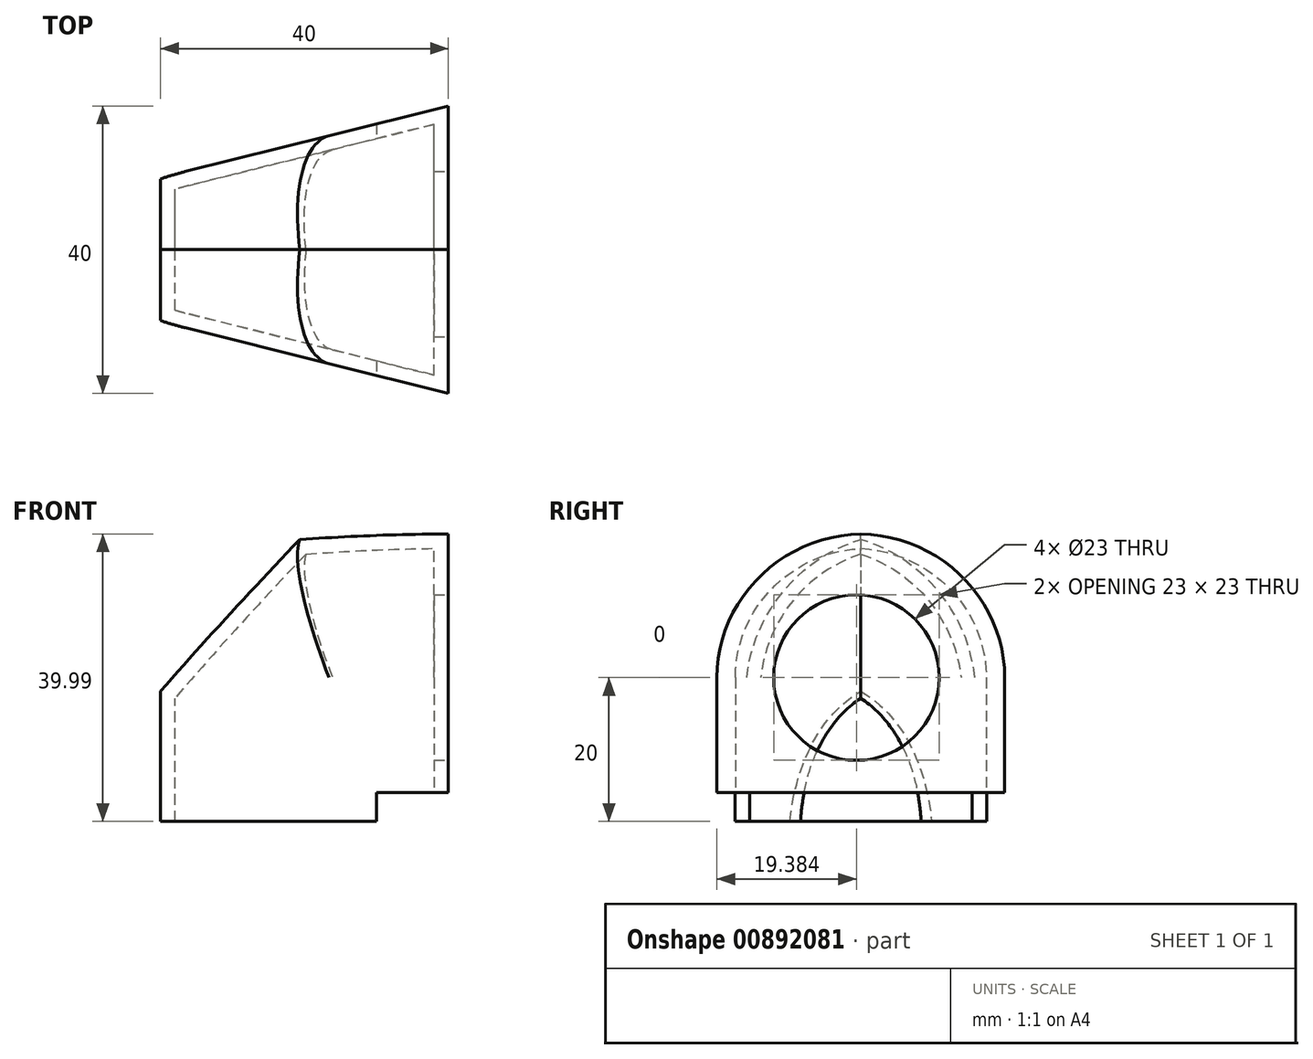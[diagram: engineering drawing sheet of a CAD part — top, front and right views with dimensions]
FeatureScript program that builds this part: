
annotation { "Feature Type Name" : "Feature", "Feature Type Description" : "" }
export const myFeature = defineFeature(function(context is Context, id is Id, definition is map)
    precondition{}
    {
        {
            var Q0;
            Q0=qCreatedBy(makeId("Top.planeOp"),FACE);
            var sketch = newSketch(context, id + "F0", { "sketchPlane" : qUnion([Q0])});
            skLineSegment(sketch, "E0", {"start": v(0, 0) * mm, "end": v(0, 40) * mm});
            skLineSegment(sketch, "E1", {"start": v(0, 20) * mm, "end": v(-79.69, 20) * mm, "construction": true});
            skLineSegment(sketch, "E2", {"start": v(-40, 10) * mm, "end": v(-40, 30) * mm});
            skLineSegment(sketch, "E3", {"start": v(-40, 30) * mm, "end": v(0, 40) * mm});
            skLineSegment(sketch, "E4", {"start": v(0, 0) * mm, "end": v(-40, 10) * mm});
            skSolve(sketch);
        }
        {
            var Q0;
            Q0=makeQuery(id+"F0.imprint","IMPRINT",FACE,{"disambiguationData":[TD([[makeQuery(id+"F0.imprint","IMPRINT",EDGE,{"derivedFrom":sQuery(id+"F0.wireOp",EDGE,"E0")}),1.0]])]});
            extrude(context, id + "F1", {"entities" : qUnion([Q0]), "depth" : 40 * mm, "offsetDistance" : 25 * mm});
        }
        {
            var Q0;
            Q0=makeQuery(id+"F1.opExtrude","CAP_EDGE",EDGE,{"disambiguationData":[OSD([sQuery(id+"F0.wireOp",EDGE,"E2")])],"isStart":false});
            chamfer(context, id + "F2", {"entities" : qUnion([Q0]), "width" : 20 * mm, "tangentPropagation" : true});
        }
        {
            var Q0;
            Q0=makeQuery(id+"F1.opExtrude","CAP_EDGE",EDGE,{"disambiguationData":[OSD([sQuery(id+"F0.wireOp",EDGE,"E3")])],"isStart":false});
            var Q1;
            Q1=makeQuery(id+"F1.opExtrude","CAP_EDGE",EDGE,{"disambiguationData":[OSD([sQuery(id+"F0.wireOp",EDGE,"E4")])],"isStart":false});
            var Q2;
            Q2=makeQuery(id+"F2.opChamfer","BLEND_EDGE",EDGE,{"blendedFrom":[makeQuery(id+"F1.opExtrude","CAP_EDGE",EDGE,{"disambiguationData":[OSD([sQuery(id+"F0.wireOp",EDGE,"E2")])],"isStart":false}),makeQuery(id+"F1.opExtrude","SWEPT_FACE",FACE,{"disambiguationData":[OSD([sQuery(id+"F0.wireOp",EDGE,"E4")])]})],"blendedInto":[makeQuery(id+"F1.opExtrude","SWEPT_FACE",FACE,{"disambiguationData":[OSD([sQuery(id+"F0.wireOp",EDGE,"E4")])]})]});
            var Q3;
            Q3=makeQuery(id+"F2.opChamfer","BLEND_EDGE",EDGE,{"blendedFrom":[makeQuery(id+"F1.opExtrude","CAP_EDGE",EDGE,{"disambiguationData":[OSD([sQuery(id+"F0.wireOp",EDGE,"E2")])],"isStart":false}),makeQuery(id+"F1.opExtrude","SWEPT_FACE",FACE,{"disambiguationData":[OSD([sQuery(id+"F0.wireOp",EDGE,"E3")])]})],"blendedInto":[makeQuery(id+"F1.opExtrude","SWEPT_FACE",FACE,{"disambiguationData":[OSD([sQuery(id+"F0.wireOp",EDGE,"E3")])]})]});
            fillet(context, id + "F3", {"entities" : qUnion([Q0, Q1, Q2, Q3]), "radius" : 20 * mm, "tangentPropagation" : true, "allowEdgeOverflow" : false});
        }
        {
            var Q0;
            Q0=makeQuery(id+"F1.opExtrude","SWEPT_FACE",FACE,{"disambiguationData":[OSD([sQuery(id+"F0.wireOp",EDGE,"E0")])]});
            var sketch = newSketch(context, id + "F4", { "sketchPlane" : qUnion([Q0])});
            skCircle(sketch, "E5", {"center": v(19.38, 20) * mm, "radius": 11.5 * mm});
            skSolve(sketch);
        }
        {
            var Q0;
            Q0=makeQuery(id+"F1.opExtrude","CAP_FACE",FACE,{"disambiguationData":[OSD([sQuery(id+"F0.wireOp",EDGE,"E0"),sQuery(id+"F0.wireOp",EDGE,"E2"),sQuery(id+"F0.wireOp",EDGE,"E3"),sQuery(id+"F0.wireOp",EDGE,"E4")])],"isStart":true});
            var Q1;
            Q1=makeQuery(id+"F1.opExtrude","SWEPT_BODY",BODY,{"disambiguationData":[OSD([sQuery(id+"F0.wireOp",EDGE,"E0"),sQuery(id+"F0.wireOp",EDGE,"E2"),sQuery(id+"F0.wireOp",EDGE,"E3"),sQuery(id+"F0.wireOp",EDGE,"E4")])]});
            shell(context, id + "F5", {"entities" : qUnion([Q0]), "parts" : qUnion([Q1]), "thickness" : 2 * mm});
        }
        {
            var Q0;
            Q0=makeQuery(id+"F4.imprint","IMPRINT",FACE,{"disambiguationData":[TD([[makeQuery(id+"F4.imprint","IMPRINT",EDGE,{"derivedFrom":sQuery(id+"F4.wireOp",EDGE,"E5")}),1.0]])]});
            extrude(context, id + "F6", {"entities" : qUnion([Q0]), "operationType" : NewBodyOperationType.REMOVE, "oppositeDirection" : true, "depth" : 5 * mm, "offsetDistance" : 25 * mm});
        }
        {
            var Q0;
            Q0=makeQuery(id+"F0.imprint","IMPRINT",FACE,{"disambiguationData":[TD([[makeQuery(id+"F0.imprint","IMPRINT",EDGE,{"derivedFrom":sQuery(id+"F0.wireOp",EDGE,"E0")}),1.0]])]});
            var sketch = newSketch(context, id + "F7", { "sketchPlane" : qUnion([Q0])});
            skLineSegment(sketch, "E6", {"start": v(-10, 0) * mm, "end": v(0, 0) * mm});
            skLineSegment(sketch, "E7", {"start": v(0, 0) * mm, "end": v(0, 40) * mm});
            skLineSegment(sketch, "E8", {"start": v(0, 40) * mm, "end": v(-10, 40) * mm});
            skLineSegment(sketch, "E9", {"start": v(-10, 40) * mm, "end": v(-10, 0) * mm});
            skSolve(sketch);
        }
        {
            var Q0;
            {var subQ3=makeQuery(id+"F0.imprint","IMPRINT",EDGE,{"derivedFrom":sQuery(id+"F0.wireOp",EDGE,"E3")});var subQ5=sQuery(id+"F7.wireOp",EDGE,"E9");var subQ7=makeQuery(id+"F7.imprint","INTERSECT",VERTEX,{"derivedFrom":[subQ3,subQ5]});Q0=makeQuery(id+"F7.imprint","IMPRINT",FACE,{"disambiguationData":[TD([[makeQuery(id+"F7.imprint","IMPRINT",EDGE,{"disambiguationData":[TD([[subQ7,-1.0]])],"derivedFrom":subQ5}),1.0]])]});}
            extrude(context, id + "F8", {"entities" : qUnion([Q0]), "operationType" : NewBodyOperationType.REMOVE, "depth" : 4 * mm, "offsetDistance" : 25 * mm});
        }
    });
